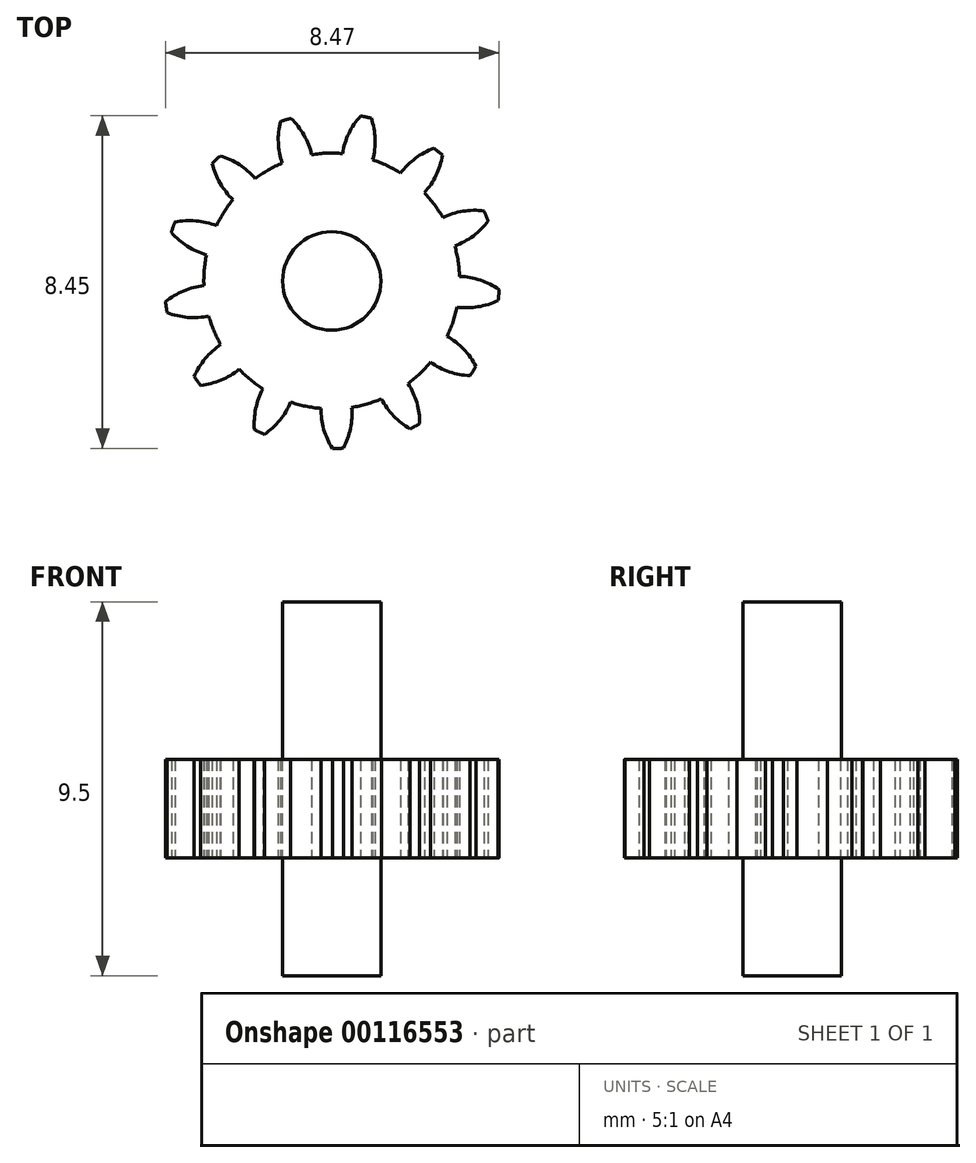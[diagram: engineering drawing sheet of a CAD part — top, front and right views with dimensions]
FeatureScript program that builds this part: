
annotation { "Feature Type Name" : "Feature", "Feature Type Description" : "" }
export const myFeature = defineFeature(function(context is Context, id is Id, definition is map)
    precondition{}
    {
        {
            var Q0;
            Q0=qCreatedBy(makeId("Top.planeOp"),FACE);
            var sketch = newSketch(context, id + "F0", { "sketchPlane" : qUnion([Q0])});
            skArc(sketch, "E0.MirrorCS", {"start": v(16.42, 19.43) * mm, "mid": v(16.94, 19.3) * mm, "end": v(17.48, 19.34) * mm});
            skArc(sketch, "E1.MirrorCS", {"start": v(16.42, 19.43) * mm, "mid": v(16.41, 19.5) * mm, "end": v(16.4, 19.57) * mm});
            skArc(sketch, "E2.MirrorCS", {"start": v(16.38, 19.7) * mm, "mid": v(16.39, 19.63) * mm, "end": v(16.4, 19.57) * mm});
            skArc(sketch, "E3.MirrorCS", {"start": v(16.38, 19.7) * mm, "mid": v(16.84, 19.98) * mm, "end": v(17.36, 20.11) * mm});
            skCircle(sketch, "E4", {"center": v(20.6, 20.23) * mm, "radius": 3.25 * mm});
            skPoint(sketch, "E4.third.point", {"position": v(23.79, 20.89) * mm});
            skLineSegment(sketch, "E5", {"start": v(17.36, 20.11) * mm, "end": v(20.6, 20.23) * mm, "construction": true});
            skLineSegment(sketch, "E6", {"start": v(17.48, 19.34) * mm, "end": v(20.6, 20.23) * mm, "construction": true});
            skArc(sketch, "E7.1.0", {"start": v(17.1, 17.8) * mm, "mid": v(17.39, 18.26) * mm, "end": v(17.78, 18.62) * mm});
            skArc(sketch, "E7.1.1", {"start": v(17.28, 17.58) * mm, "mid": v(17.8, 17.71) * mm, "end": v(18.25, 18) * mm});
            skArc(sketch, "E7.1.2", {"start": v(17.28, 17.58) * mm, "mid": v(17.23, 17.63) * mm, "end": v(17.19, 17.69) * mm});
            skArc(sketch, "E7.1.3", {"start": v(17.1, 17.8) * mm, "mid": v(17.15, 17.74) * mm, "end": v(17.19, 17.69) * mm});
            skArc(sketch, "E7.2.0", {"start": v(18.64, 16.46) * mm, "mid": v(18.67, 16.99) * mm, "end": v(18.86, 17.5) * mm});
            skArc(sketch, "E7.2.1", {"start": v(18.89, 16.34) * mm, "mid": v(19.28, 16.7) * mm, "end": v(19.56, 17.15) * mm});
            skArc(sketch, "E7.2.2", {"start": v(18.89, 16.34) * mm, "mid": v(18.83, 16.36) * mm, "end": v(18.76, 16.4) * mm});
            skArc(sketch, "E7.2.3", {"start": v(18.64, 16.46) * mm, "mid": v(18.7, 16.42) * mm, "end": v(18.76, 16.4) * mm});
            skArc(sketch, "E7.3.0", {"start": v(20.62, 15.98) * mm, "mid": v(20.4, 16.46) * mm, "end": v(20.33, 17) * mm});
            skArc(sketch, "E7.3.1", {"start": v(20.9, 15.99) * mm, "mid": v(21.08, 16.49) * mm, "end": v(21.11, 17.02) * mm});
            skArc(sketch, "E7.3.2", {"start": v(20.9, 15.99) * mm, "mid": v(20.83, 15.98) * mm, "end": v(20.76, 15.98) * mm});
            skArc(sketch, "E7.3.3", {"start": v(20.62, 15.98) * mm, "mid": v(20.69, 15.98) * mm, "end": v(20.76, 15.98) * mm});
            skArc(sketch, "E7.4.0", {"start": v(22.6, 16.47) * mm, "mid": v(22.17, 16.8) * mm, "end": v(21.87, 17.24) * mm});
            skArc(sketch, "E7.4.1", {"start": v(22.84, 16.6) * mm, "mid": v(22.76, 17.14) * mm, "end": v(22.54, 17.63) * mm});
            skArc(sketch, "E7.4.2", {"start": v(22.84, 16.6) * mm, "mid": v(22.78, 16.57) * mm, "end": v(22.72, 16.54) * mm});
            skArc(sketch, "E7.4.3", {"start": v(22.6, 16.47) * mm, "mid": v(22.66, 16.5) * mm, "end": v(22.72, 16.54) * mm});
            skArc(sketch, "E7.5.0", {"start": v(24.11, 17.83) * mm, "mid": v(23.59, 17.92) * mm, "end": v(23.11, 18.17) * mm});
            skArc(sketch, "E7.5.1", {"start": v(24.26, 18.06) * mm, "mid": v(23.95, 18.5) * mm, "end": v(23.53, 18.83) * mm});
            skArc(sketch, "E7.5.2", {"start": v(24.26, 18.06) * mm, "mid": v(24.23, 18) * mm, "end": v(24.2, 17.94) * mm});
            skArc(sketch, "E7.5.3", {"start": v(24.11, 17.83) * mm, "mid": v(24.15, 17.88) * mm, "end": v(24.2, 17.94) * mm});
            skArc(sketch, "E7.6.0", {"start": v(24.83, 19.73) * mm, "mid": v(24.32, 19.58) * mm, "end": v(23.78, 19.57) * mm});
            skArc(sketch, "E7.6.1", {"start": v(24.85, 20.01) * mm, "mid": v(24.38, 20.25) * mm, "end": v(23.85, 20.35) * mm});
            skArc(sketch, "E7.6.2", {"start": v(24.85, 20.01) * mm, "mid": v(24.85, 19.94) * mm, "end": v(24.85, 19.87) * mm});
            skArc(sketch, "E7.6.3", {"start": v(24.83, 19.73) * mm, "mid": v(24.84, 19.8) * mm, "end": v(24.85, 19.87) * mm});
            skArc(sketch, "E7.7.0", {"start": v(24.58, 21.75) * mm, "mid": v(24.2, 21.38) * mm, "end": v(23.73, 21.12) * mm});
            skArc(sketch, "E7.7.1", {"start": v(24.47, 22.01) * mm, "mid": v(23.94, 22) * mm, "end": v(23.42, 21.84) * mm});
            skArc(sketch, "E7.7.2", {"start": v(24.47, 22.01) * mm, "mid": v(24.5, 21.95) * mm, "end": v(24.53, 21.88) * mm});
            skArc(sketch, "E7.7.3", {"start": v(24.58, 21.75) * mm, "mid": v(24.55, 21.82) * mm, "end": v(24.53, 21.88) * mm});
            skArc(sketch, "E7.8.0", {"start": v(23.41, 23.43) * mm, "mid": v(23.25, 22.92) * mm, "end": v(22.96, 22.47) * mm});
            skArc(sketch, "E7.8.1", {"start": v(23.2, 23.6) * mm, "mid": v(22.73, 23.35) * mm, "end": v(22.35, 22.97) * mm});
            skArc(sketch, "E7.8.2", {"start": v(23.2, 23.6) * mm, "mid": v(23.25, 23.56) * mm, "end": v(23.3, 23.52) * mm});
            skArc(sketch, "E7.8.3", {"start": v(23.41, 23.43) * mm, "mid": v(23.36, 23.47) * mm, "end": v(23.3, 23.52) * mm});
            skArc(sketch, "E7.9.0", {"start": v(21.6, 24.37) * mm, "mid": v(21.7, 23.84) * mm, "end": v(21.64, 23.31) * mm});
            skArc(sketch, "E7.9.1", {"start": v(21.33, 24.43) * mm, "mid": v(21.04, 23.98) * mm, "end": v(20.88, 23.47) * mm});
            skArc(sketch, "E7.9.2", {"start": v(21.33, 24.43) * mm, "mid": v(21.4, 24.41) * mm, "end": v(21.47, 24.4) * mm});
            skArc(sketch, "E7.9.3", {"start": v(21.6, 24.37) * mm, "mid": v(21.54, 24.38) * mm, "end": v(21.47, 24.4) * mm});
            skArc(sketch, "E7.10.0", {"start": v(19.57, 24.36) * mm, "mid": v(19.9, 23.94) * mm, "end": v(20.1, 23.44) * mm});
            skArc(sketch, "E7.10.1", {"start": v(19.3, 24.28) * mm, "mid": v(19.25, 23.75) * mm, "end": v(19.34, 23.23) * mm});
            skArc(sketch, "E7.10.2", {"start": v(19.3, 24.28) * mm, "mid": v(19.37, 24.3) * mm, "end": v(19.44, 24.33) * mm});
            skArc(sketch, "E7.10.3", {"start": v(19.57, 24.36) * mm, "mid": v(19.5, 24.34) * mm, "end": v(19.44, 24.33) * mm});
            skArc(sketch, "E7.11.0", {"start": v(17.77, 23.4) * mm, "mid": v(18.26, 23.19) * mm, "end": v(18.66, 22.84) * mm});
            skArc(sketch, "E7.11.1", {"start": v(17.57, 23.22) * mm, "mid": v(17.76, 22.72) * mm, "end": v(18.1, 22.3) * mm});
            skArc(sketch, "E7.11.2", {"start": v(17.57, 23.22) * mm, "mid": v(17.62, 23.27) * mm, "end": v(17.67, 23.31) * mm});
            skArc(sketch, "E7.11.3", {"start": v(17.77, 23.4) * mm, "mid": v(17.72, 23.36) * mm, "end": v(17.67, 23.31) * mm});
            skArc(sketch, "E7.12.0", {"start": v(16.62, 21.73) * mm, "mid": v(17.15, 21.76) * mm, "end": v(17.67, 21.64) * mm});
            skArc(sketch, "E7.12.1", {"start": v(16.53, 21.46) * mm, "mid": v(16.93, 21.11) * mm, "end": v(17.42, 20.9) * mm});
            skArc(sketch, "E7.12.2", {"start": v(16.53, 21.46) * mm, "mid": v(16.55, 21.53) * mm, "end": v(16.57, 21.6) * mm});
            skArc(sketch, "E7.12.3", {"start": v(16.62, 21.73) * mm, "mid": v(16.6, 21.66) * mm, "end": v(16.57, 21.6) * mm});
            skSolve(sketch);
        }
        {
            var Q0;
            Q0 = qSketchRegion(id + "F0", true);
            extrude(context, id + "F1", {"entities" : qUnion([Q0]), "depth" : 2.5 * mm});
        }
        {
            var Q0;
            Q0=makeQuery(id+"F1.opExtrude","CAP_FACE",FACE,{"disambiguationData":[OSD([sQuery(id+"F0.wireOp",EDGE,"E0.MirrorCS"),sQuery(id+"F0.wireOp",EDGE,"E1.MirrorCS"),sQuery(id+"F0.wireOp",EDGE,"E2.MirrorCS"),sQuery(id+"F0.wireOp",EDGE,"E3.MirrorCS"),sQuery(id+"F0.wireOp",EDGE,"794cd6ff-f0c4-4845-9346-57aea4890d9c"),sQuery(id+"F0.wireOp",EDGE,"76696015-720e-409f-8f05-ba0af8492f54.1.0"),sQuery(id+"F0.wireOp",EDGE,"76696015-720e-409f-8f05-ba0af8492f54.1.1"),sQuery(id+"F0.wireOp",EDGE,"76696015-720e-409f-8f05-ba0af8492f54.1.2"),sQuery(id+"F0.wireOp",EDGE,"76696015-720e-409f-8f05-ba0af8492f54.1.3"),sQuery(id+"F0.wireOp",EDGE,"76696015-720e-409f-8f05-ba0af8492f54.2.0"),sQuery(id+"F0.wireOp",EDGE,"76696015-720e-409f-8f05-ba0af8492f54.2.1"),sQuery(id+"F0.wireOp",EDGE,"76696015-720e-409f-8f05-ba0af8492f54.2.2"),sQuery(id+"F0.wireOp",EDGE,"76696015-720e-409f-8f05-ba0af8492f54.2.3"),sQuery(id+"F0.wireOp",EDGE,"76696015-720e-409f-8f05-ba0af8492f54.3.0"),sQuery(id+"F0.wireOp",EDGE,"76696015-720e-409f-8f05-ba0af8492f54.3.1"),sQuery(id+"F0.wireOp",EDGE,"76696015-720e-409f-8f05-ba0af8492f54.3.2"),sQuery(id+"F0.wireOp",EDGE,"76696015-720e-409f-8f05-ba0af8492f54.3.3"),sQuery(id+"F0.wireOp",EDGE,"76696015-720e-409f-8f05-ba0af8492f54.4.0"),sQuery(id+"F0.wireOp",EDGE,"76696015-720e-409f-8f05-ba0af8492f54.4.1"),sQuery(id+"F0.wireOp",EDGE,"76696015-720e-409f-8f05-ba0af8492f54.4.2"),sQuery(id+"F0.wireOp",EDGE,"76696015-720e-409f-8f05-ba0af8492f54.4.3"),sQuery(id+"F0.wireOp",EDGE,"76696015-720e-409f-8f05-ba0af8492f54.5.0"),sQuery(id+"F0.wireOp",EDGE,"76696015-720e-409f-8f05-ba0af8492f54.5.1"),sQuery(id+"F0.wireOp",EDGE,"76696015-720e-409f-8f05-ba0af8492f54.5.2"),sQuery(id+"F0.wireOp",EDGE,"76696015-720e-409f-8f05-ba0af8492f54.5.3"),sQuery(id+"F0.wireOp",EDGE,"76696015-720e-409f-8f05-ba0af8492f54.6.0"),sQuery(id+"F0.wireOp",EDGE,"76696015-720e-409f-8f05-ba0af8492f54.6.1"),sQuery(id+"F0.wireOp",EDGE,"76696015-720e-409f-8f05-ba0af8492f54.6.2"),sQuery(id+"F0.wireOp",EDGE,"76696015-720e-409f-8f05-ba0af8492f54.6.3"),sQuery(id+"F0.wireOp",EDGE,"76696015-720e-409f-8f05-ba0af8492f54.7.0"),sQuery(id+"F0.wireOp",EDGE,"76696015-720e-409f-8f05-ba0af8492f54.7.1"),sQuery(id+"F0.wireOp",EDGE,"76696015-720e-409f-8f05-ba0af8492f54.7.2"),sQuery(id+"F0.wireOp",EDGE,"76696015-720e-409f-8f05-ba0af8492f54.7.3"),sQuery(id+"F0.wireOp",EDGE,"76696015-720e-409f-8f05-ba0af8492f54.8.0"),sQuery(id+"F0.wireOp",EDGE,"76696015-720e-409f-8f05-ba0af8492f54.8.1"),sQuery(id+"F0.wireOp",EDGE,"76696015-720e-409f-8f05-ba0af8492f54.8.2"),sQuery(id+"F0.wireOp",EDGE,"76696015-720e-409f-8f05-ba0af8492f54.8.3"),sQuery(id+"F0.wireOp",EDGE,"76696015-720e-409f-8f05-ba0af8492f54.9.0"),sQuery(id+"F0.wireOp",EDGE,"76696015-720e-409f-8f05-ba0af8492f54.9.1"),sQuery(id+"F0.wireOp",EDGE,"76696015-720e-409f-8f05-ba0af8492f54.9.2"),sQuery(id+"F0.wireOp",EDGE,"76696015-720e-409f-8f05-ba0af8492f54.9.3"),sQuery(id+"F0.wireOp",EDGE,"76696015-720e-409f-8f05-ba0af8492f54.10.0"),sQuery(id+"F0.wireOp",EDGE,"76696015-720e-409f-8f05-ba0af8492f54.10.1"),sQuery(id+"F0.wireOp",EDGE,"76696015-720e-409f-8f05-ba0af8492f54.10.2"),sQuery(id+"F0.wireOp",EDGE,"76696015-720e-409f-8f05-ba0af8492f54.10.3"),sQuery(id+"F0.wireOp",EDGE,"76696015-720e-409f-8f05-ba0af8492f54.11.0"),sQuery(id+"F0.wireOp",EDGE,"76696015-720e-409f-8f05-ba0af8492f54.11.1"),sQuery(id+"F0.wireOp",EDGE,"76696015-720e-409f-8f05-ba0af8492f54.11.2"),sQuery(id+"F0.wireOp",EDGE,"76696015-720e-409f-8f05-ba0af8492f54.11.3"),sQuery(id+"F0.wireOp",EDGE,"76696015-720e-409f-8f05-ba0af8492f54.12.0"),sQuery(id+"F0.wireOp",EDGE,"76696015-720e-409f-8f05-ba0af8492f54.12.1"),sQuery(id+"F0.wireOp",EDGE,"76696015-720e-409f-8f05-ba0af8492f54.12.2"),sQuery(id+"F0.wireOp",EDGE,"76696015-720e-409f-8f05-ba0af8492f54.12.3"),sQuery(id+"F0.wireOp",EDGE,"76696015-720e-409f-8f05-ba0af8492f54.13.0"),sQuery(id+"F0.wireOp",EDGE,"76696015-720e-409f-8f05-ba0af8492f54.13.1"),sQuery(id+"F0.wireOp",EDGE,"76696015-720e-409f-8f05-ba0af8492f54.13.2"),sQuery(id+"F0.wireOp",EDGE,"76696015-720e-409f-8f05-ba0af8492f54.13.3")])],"isStart":false});
            var sketch = newSketch(context, id + "F2", { "sketchPlane" : qUnion([Q0])});
            skCircle(sketch, "E8", {"center": v(20.6, 20.23) * mm, "radius": 1.25 * mm});
            skSolve(sketch);
        }
        {
            var Q0;
            Q0 = qSketchRegion(id + "F2", true);
            extrude(context, id + "F3", {"entities" : qUnion([Q0]), "operationType" : NewBodyOperationType.ADD, "depth" : 4 * mm, "hasSecondDirection" : true, "secondDirectionOppositeDirection" : true, "secondDirectionDepth" : 5.5 * mm});
        }
    });
